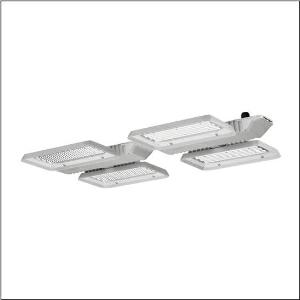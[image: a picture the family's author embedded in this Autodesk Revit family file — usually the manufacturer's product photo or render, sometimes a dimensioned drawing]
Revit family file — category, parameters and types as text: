
# Revit family: highbay_11_51hla1d24mca
name_source: partatom
category: Lighting Fixtures
units: mm (PartAtom-declared; Revit-internal decimal feet)

## family parameters
Cut with Voids When Loaded = No
Host = Face
Light Source = No
Part Type = Normal
Room Calculation Point = No
Round Connector Dimension = Use Diameter
Shared = No

## types (1)
- --- (1 x LED, 28120 lm, 162.4 W, 4000K)
    Apparent Load = 162 VA
    CIE Flux Codes = 88 95 99 100 99
    Color Rendering = 80
    Color Temperature = 4000K
    Default Elevation = 1800 mm
    Description = Highbay 11, LED high bay luminaire, primary light control with lens, of PMMA, light emission: direct distribution, primary light characteristic: symmetric, installation type: suspended mounting, surface-mounted, for 2x 2x LED, rated luminous flux: 28.120lm, luminous efficacy: 173lm/W, light colour: 840, colour temperature: 4000K, control gear: ECG DALI, with terminal, 5-pole, max. 2.5mm², mains connection: 230..240V, AC, 50/60Hz, rated input power: 162W, LED unit, of diecast aluminium, unplated, bead blasted, silver, length: 940mm, width: 500mm, height: 65mm, housing, of diecast aluminium, uncoated, bead blasted, silver, protection rating (complete): IP65, insulation class (complete): insulation class I (protective earthing), certification: CE, ENEC, VDE, UKCA, protection symbol: D, impact resistance: IK08 with glass or PC cover, permissible operating ambient temperature: -35..+55°C, reducing of maximum allowable ambient temperature of 5°C with ceiling mounting, corresponds to IFS (International Featured Standards) requirements for safety and quality in the food industry, packaging unit: 1 piece
    Height = 95 mm
    Lamp = 1 x LED
    Lamp Light Flux = 28120 lm
    Lamp Power = 162.4 W
    Lamp count = 1
    Length = 939 mm
    Luminous efficacy = 173 lm/W
    Manufacturer = Siteco
    ModVariant = No
    Model = 51HLA1D24MCA
    Mounting Place = Ceiling
    Mounting Type = Pendant
    Number of Poles = 1
    OnlyDefault = Yes
    Power Factor = 1
    Product Name = Highbay 11
    Product group = LED high bay luminaire
    ProductGroupID = 903
    Protection Class = Protection class I
    Protection Degree = IP 65
    RLX_Detail_Level = 1
    RLX_Emergency_Light_Flux = 0 lm
    RLX_Emergency_Type = 0
    RLX_Emergency_Type_DB = No
    RlxData = <blob elided: 100329 chars, md5=5fea903c>
    Socket = socket
    Standby Power = 0 W
    System Light Flux = 28120 lm
    System Power = 162 W
    Type Comments = factory setting: luminous flux: 100 % | dim-lin: 254 | 460 mA
    Type Image = l_1003428.jpg
    URL = http://relux.com
    VarID = @adj_160293
    Voltage = 0 V
    Weight = 0.00 kg
    Width = 501 mm

## geometry (parser evidence)
native form markers: Blend x4, Sweep x12
no freeform markers — native parametric forms only
